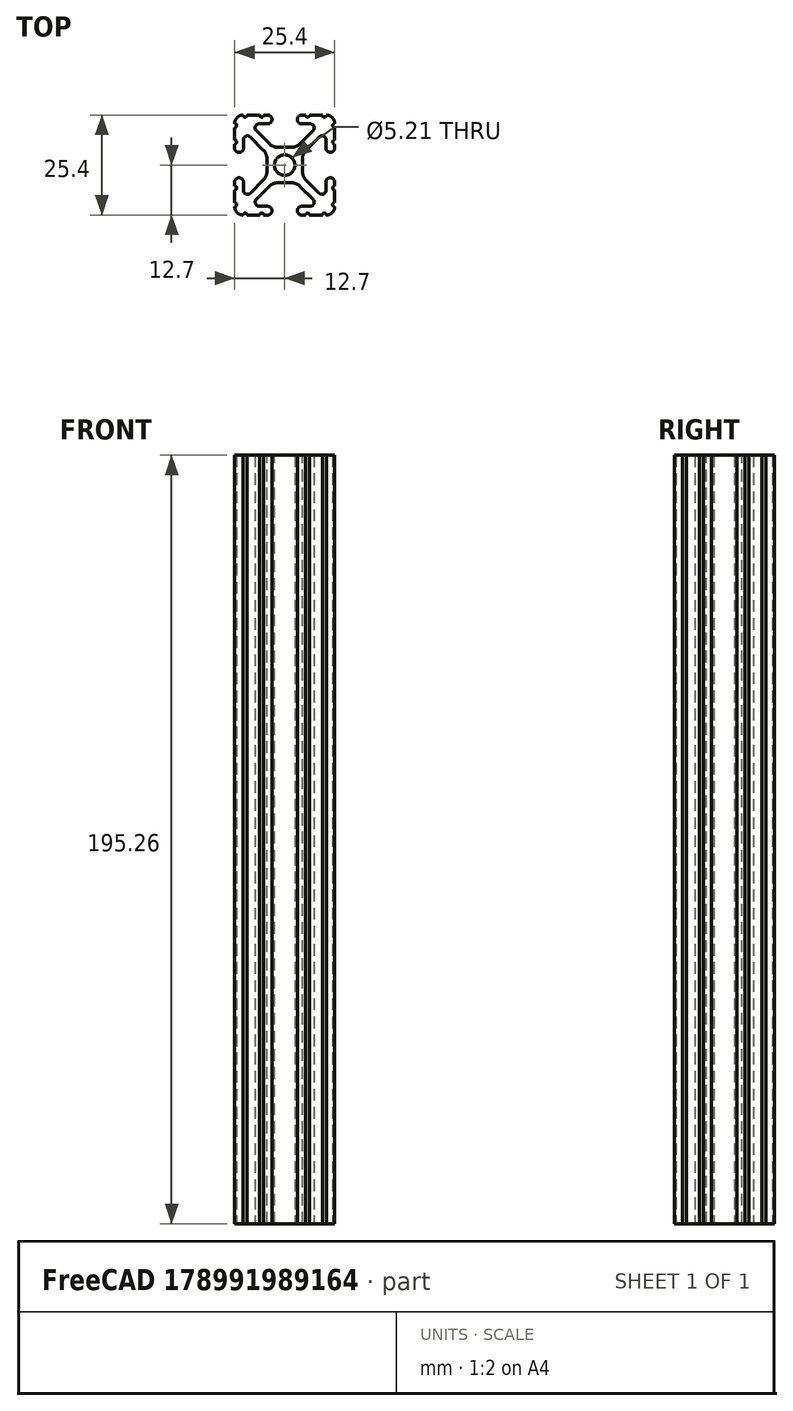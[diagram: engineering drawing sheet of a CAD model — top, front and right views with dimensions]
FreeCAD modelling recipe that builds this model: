
FCSTD DOCUMENT  (FreeCAD 0.19R24267 (Git))
Label: 1010-7p6875
License: All rights reserved
LicenseURL: http://en.wikipedia.org/wiki/All_rights_reserved
objects: Sketcher::SketchObject×1, Part::Extrusion×1
note: 2 computed .brp shape members not serialized (recipe doc carries the construction recipe); baked Part::Feature solids carry a one-line shape summary decoded from their .brp

FEATURE [Sketcher::SketchObject] Sketch097
  FullyConstrained = false
  sketch-geometry (97):
    g0: Circle CenterX=0 CenterY=0 CenterZ=0 NormalX=0 NormalY=0 NormalZ=-1 AngleXU=0 Radius=2.6035
    g1: ArcOfCircle CenterX=12.7 CenterY=5.82508 CenterZ=0 NormalX=0 NormalY=0 NormalZ=1 AngleXU=0 Radius=0.508 StartAngle=1.5708 EndAngle=4.71239
    g2: LineSegment StartX=3.2385 StartY=11.651 StartZ=0 EndX=3.2385 EndY=11.5392 EndZ=0
    g3: LineSegment StartX=6.33313 StartY=-12.7 StartZ=0 EndX=9.55044 EndY=-12.7 EndZ=0
    g4: LineSegment StartX=7.20704 StartY=8.72437 StartZ=0 EndX=3.89827 EndY=5.42317 EndZ=0
    g5: ArcOfCircle CenterX=7.6835 CenterY=1.59319 CenterZ=0 NormalX=0 NormalY=0 NormalZ=1 AngleXU=0 Radius=3.175 StartAngle=2.35505 EndAngle=3.14159
    g6: ArcOfCircle CenterX=-1.70925 CenterY=-7.6708 CenterZ=0 NormalX=0 NormalY=0 NormalZ=1 AngleXU=0 Radius=3.175 StartAngle=1.5708 EndAngle=2.35528
    g7: ArcOfCircle CenterX=11.5392 CenterY=-4.28747 CenterZ=0 NormalX=0 NormalY=0 NormalZ=1 AngleXU=0 Radius=1.04901 StartAngle=1.5708 EndAngle=3.14159
    g8: ArcOfCircle CenterX=12.7 CenterY=-5.82508 CenterZ=0 NormalX=0 NormalY=0 NormalZ=1 AngleXU=0 Radius=0.508 StartAngle=1.5708 EndAngle=4.71239
    g9: LineSegment StartX=4.28751 StartY=10.4902 StartZ=0 EndX=6.47679 EndY=10.4902 EndZ=0
    g10: ArcOfCircle CenterX=4.28751 CenterY=11.651 CenterZ=0 NormalX=0 NormalY=0 NormalZ=1 AngleXU=0 Radius=1.04901 StartAngle=1.5708 EndAngle=3.14159
    g11: ArcOfCircle CenterX=6.47679 CenterY=9.45629 CenterZ=0 NormalX=0 NormalY=0 NormalZ=1 AngleXU=0 Radius=1.03391 StartAngle=5.49664 EndAngle=7.85398
    g12: ArcOfCircle CenterX=4.28751 CenterY=11.5392 CenterZ=0 NormalX=0 NormalY=0 NormalZ=1 AngleXU=0 Radius=1.04901 StartAngle=3.14159 EndAngle=4.71239
    g13: LineSegment StartX=3.95227 StartY=-5.42369 StartZ=0 EndX=7.17965 EndY=-8.64519 EndZ=0
    g14: ArcOfCircle CenterX=11.651 CenterY=4.28747 CenterZ=0 NormalX=0 NormalY=0 NormalZ=1 AngleXU=0 Radius=1.04901 StartAngle=4.71239 EndAngle=6.28319
    g15: ArcOfCircle CenterX=-5.82513 CenterY=-12.7 CenterZ=0 NormalX=0 NormalY=0 NormalZ=1 AngleXU=0 Radius=0.508 StartAngle=0 EndAngle=3.14159
    g16: LineSegment StartX=-6.47679 StartY=10.4902 StartZ=0 EndX=-4.28751 EndY=10.4902 EndZ=0
    g17: ArcOfCircle CenterX=-12.7 CenterY=10.0584 CenterZ=0 NormalX=0 NormalY=0 NormalZ=1 AngleXU=0 Radius=0.508 StartAngle=4.71239 EndAngle=7.85368
    g18: ArcOfCircle CenterX=-12.7 CenterY=5.82508 CenterZ=0 NormalX=0 NormalY=0 NormalZ=1 AngleXU=0 Radius=0.508 StartAngle=4.71239 EndAngle=7.85398
    g19: LineSegment StartX=-11.5392 StartY=-3.23846 StartZ=0 EndX=-11.651 EndY=-3.23846 EndZ=0
    g20: LineSegment StartX=-3.89827 StartY=5.42317 StartZ=0 EndX=-7.20704 EndY=8.72437 EndZ=0
    g21: LineSegment StartX=1.65578 StartY=4.4958 StartZ=0 EndX=-1.65578 EndY=4.4958 EndZ=0
    g22: ArcOfCircle CenterX=-1.65578 CenterY=7.6708 CenterZ=0 NormalX=0 NormalY=0 NormalZ=1 AngleXU=0 Radius=3.175 StartAngle=3.92813 EndAngle=4.71239
    g23: LineSegment StartX=-9.55044 StartY=-12.7 StartZ=0 EndX=-6.33313 EndY=-12.7 EndZ=0
    g24: ArcOfCircle CenterX=-5.82513 CenterY=12.7 CenterZ=0 NormalX=0 NormalY=0 NormalZ=1 AngleXU=0 Radius=0.508 StartAngle=3.14159 EndAngle=6.28319
    g25: ArcOfCircle CenterX=-4.28751 CenterY=11.651 CenterZ=0 NormalX=0 NormalY=0 NormalZ=1 AngleXU=0 Radius=1.04901 StartAngle=0 EndAngle=1.5708
    g26: LineSegment StartX=-12.7 StartY=-4.28747 StartZ=0 EndX=-12.7 EndY=-5.31708 EndZ=0
    g27: ArcOfCircle CenterX=-6.47679 CenterY=9.45629 CenterZ=0 NormalX=0 NormalY=0 NormalZ=1 AngleXU=0 Radius=1.03391 StartAngle=1.5708 EndAngle=3.92813
    g28: ArcOfCircle CenterX=-4.28751 CenterY=11.5392 CenterZ=0 NormalX=0 NormalY=0 NormalZ=1 AngleXU=0 Radius=1.04901 StartAngle=4.71239 EndAngle=6.28319
    g29: LineSegment StartX=-5.44101 StartY=-3.84082 StartZ=0 EndX=-8.73713 EndY=-7.12941 EndZ=0
    g30: ArcOfCircle CenterX=-7.6835 CenterY=-1.59319 CenterZ=0 NormalX=0 NormalY=0 NormalZ=1 AngleXU=0 Radius=3.175 StartAngle=5.49664 EndAngle=6.28319
    g31: LineSegment StartX=-12.7 StartY=5.31708 StartZ=0 EndX=-12.7 EndY=4.28747 EndZ=0
    g32: LineSegment StartX=-8.73713 StartY=7.12941 StartZ=0 EndX=-5.44101 EndY=3.84082 EndZ=0
    g33: LineSegment StartX=-11.651 StartY=3.23846 StartZ=0 EndX=-11.5392 EndY=3.23846 EndZ=0
    g34: ArcOfCircle CenterX=-9.46279 CenterY=-6.40209 CenterZ=0 NormalX=0 NormalY=0 NormalZ=1 AngleXU=0 Radius=1.02741 StartAngle=3.14159 EndAngle=5.49664
    g35: ArcOfCircle CenterX=-10.5918 CenterY=10.5918 CenterZ=0 NormalX=0 NormalY=0 NormalZ=1 AngleXU=0 Radius=2.1082 StartAngle=1.55877 EndAngle=3.15364
    g36: LineSegment StartX=-12.7 StartY=9.5504 StartZ=0 EndX=-12.7 EndY=6.33308 EndZ=0
    g37: LineSegment StartX=-6.33313 StartY=12.7 StartZ=0 EndX=-9.55044 EndY=12.7 EndZ=0
    g38: ArcOfCircle CenterX=-11.5392 CenterY=-4.28747 CenterZ=0 NormalX=0 NormalY=0 NormalZ=1 AngleXU=0 Radius=1.04901 StartAngle=0 EndAngle=1.5708
    g39: LineSegment StartX=4.28751 StartY=-12.7 StartZ=0 EndX=5.31713 EndY=-12.7 EndZ=0
    g40: LineSegment StartX=5.44101 StartY=3.84082 StartZ=0 EndX=8.73713 EndY=7.12941 EndZ=0
    g41: LineSegment StartX=10.4902 StartY=-4.28747 StartZ=0 EndX=10.4902 EndY=-6.40209 EndZ=0
    g42: ArcOfCircle CenterX=9.46279 CenterY=6.40209 CenterZ=0 NormalX=0 NormalY=0 NormalZ=1 AngleXU=0 Radius=1.02741 StartAngle=0 EndAngle=2.35505
    g43: ArcOfCircle CenterX=5.82513 CenterY=-12.7 CenterZ=0 NormalX=0 NormalY=0 NormalZ=1 AngleXU=0 Radius=0.508 StartAngle=0 EndAngle=3.14159
    g44: LineSegment StartX=12.7 StartY=-9.5504 StartZ=0 EndX=12.7 EndY=-6.33308 EndZ=0
    g45: LineSegment StartX=4.5085 StartY=-1.59319 StartZ=0 EndX=4.5085 EndY=1.59319 EndZ=0
    g46: ArcOfCircle CenterX=12.7 CenterY=10.0584 CenterZ=0 NormalX=0 NormalY=0 NormalZ=1 AngleXU=0 Radius=0.508 StartAngle=1.5711 EndAngle=4.71239
    g47: ArcOfCircle CenterX=12.7 CenterY=-10.0584 CenterZ=0 NormalX=0 NormalY=0 NormalZ=1 AngleXU=0 Radius=0.508 StartAngle=1.5708 EndAngle=4.71209
    g48: LineSegment StartX=3.2385 StartY=-11.5392 StartZ=0 EndX=3.2385 EndY=-11.651 EndZ=0
    g49: LineSegment StartX=8.73713 StartY=-7.12941 StartZ=0 EndX=5.44101 EndY=-3.84082 EndZ=0
    g50: ArcOfCircle CenterX=11.651 CenterY=-4.28747 CenterZ=0 NormalX=0 NormalY=0 NormalZ=1 AngleXU=0 Radius=1.04901 StartAngle=0 EndAngle=1.5708
    g51: ArcOfCircle CenterX=1.65578 CenterY=7.6708 CenterZ=0 NormalX=0 NormalY=0 NormalZ=1 AngleXU=0 Radius=3.175 StartAngle=4.71239 EndAngle=5.49664
    g52: ArcOfCircle CenterX=7.6835 CenterY=-1.59319 CenterZ=0 NormalX=0 NormalY=0 NormalZ=1 AngleXU=0 Radius=3.175 StartAngle=3.14159 EndAngle=3.92813
    g53: LineSegment StartX=12.7 StartY=4.28747 StartZ=0 EndX=12.7 EndY=5.31708 EndZ=0
    g54: ArcOfCircle CenterX=6.41641 CenterY=-9.40983 CenterZ=0 NormalX=0 NormalY=0 NormalZ=1 AngleXU=0 Radius=1.08037 StartAngle=4.71239 EndAngle=7.06949
    g55: LineSegment StartX=12.7 StartY=-5.31708 StartZ=0 EndX=12.7 EndY=-4.28747 EndZ=0
    g56: ArcOfCircle CenterX=10.0584 CenterY=-12.7 CenterZ=0 NormalX=0 NormalY=0 NormalZ=1 AngleXU=0 Radius=0.508 StartAngle=0.000300194 EndAngle=3.14159
    g57: ArcOfCircle CenterX=11.5392 CenterY=4.28747 CenterZ=0 NormalX=0 NormalY=0 NormalZ=1 AngleXU=0 Radius=1.04901 StartAngle=3.14159 EndAngle=4.71239
    g58: LineSegment StartX=12.7 StartY=6.33308 StartZ=0 EndX=12.7 EndY=9.5504 EndZ=0
    g59: ArcOfCircle CenterX=4.28751 CenterY=-11.5392 CenterZ=0 NormalX=0 NormalY=0 NormalZ=1 AngleXU=0 Radius=1.04901 StartAngle=1.5708 EndAngle=3.14159
    g60: ArcOfCircle CenterX=10.5918 CenterY=10.5918 CenterZ=0 NormalX=0 NormalY=0 NormalZ=1 AngleXU=0 Radius=2.1082 StartAngle=6.27114 EndAngle=7.86601
    g61: ArcOfCircle CenterX=9.46279 CenterY=-6.40209 CenterZ=0 NormalX=0 NormalY=0 NormalZ=1 AngleXU=0 Radius=1.02741 StartAngle=3.92813 EndAngle=6.28319
    g62: LineSegment StartX=6.41641 StartY=-10.4902 StartZ=0 EndX=4.28751 EndY=-10.4902 EndZ=0
    g63: LineSegment StartX=-10.4902 StartY=-6.40209 StartZ=0 EndX=-10.4902 EndY=-4.28747 EndZ=0
    g64: ArcOfCircle CenterX=-9.46279 CenterY=6.40209 CenterZ=0 NormalX=0 NormalY=0 NormalZ=1 AngleXU=0 Radius=1.02741 StartAngle=0.786542 EndAngle=3.14159
    g65: LineSegment StartX=-10.4902 StartY=4.28747 StartZ=0 EndX=-10.4902 EndY=6.40209 EndZ=0
    g66: LineSegment StartX=-4.5085 StartY=1.59319 StartZ=0 EndX=-4.5085 EndY=-1.59319 EndZ=0
    g67: LineSegment StartX=-4.28751 StartY=12.7 StartZ=0 EndX=-5.31713 EndY=12.7 EndZ=0
    g68: ArcOfCircle CenterX=-11.5392 CenterY=4.28747 CenterZ=0 NormalX=0 NormalY=0 NormalZ=1 AngleXU=0 Radius=1.04901 StartAngle=4.71239 EndAngle=6.28319
    g69: LineSegment StartX=-3.2385 StartY=11.5392 StartZ=0 EndX=-3.2385 EndY=11.651 EndZ=0
    g70: ArcOfCircle CenterX=-11.651 CenterY=4.28747 CenterZ=0 NormalX=0 NormalY=0 NormalZ=1 AngleXU=0 Radius=1.04901 StartAngle=3.14159 EndAngle=4.71239
    g71: ArcOfCircle CenterX=-7.6835 CenterY=1.59319 CenterZ=0 NormalX=0 NormalY=0 NormalZ=1 AngleXU=0 Radius=3.175 StartAngle=0 EndAngle=0.786542
    g72: ArcOfCircle CenterX=-10.0584 CenterY=12.7 CenterZ=0 NormalX=0 NormalY=0 NormalZ=1 AngleXU=0 Radius=0.508 StartAngle=3.14189 EndAngle=6.28319
    g73: LineSegment StartX=-1.70925 StartY=-4.4958 StartZ=0 EndX=1.70925 EndY=-4.4958 EndZ=0
    g74: LineSegment StartX=11.651 StartY=-3.23846 StartZ=0 EndX=11.5392 EndY=-3.23846 EndZ=0
    g75: ArcOfCircle CenterX=-10.5918 CenterY=-10.5918 CenterZ=0 NormalX=0 NormalY=0 NormalZ=1 AngleXU=0 Radius=2.1082 StartAngle=3.12954 EndAngle=4.72442
    g76: ArcOfCircle CenterX=10.5918 CenterY=-10.5918 CenterZ=0 NormalX=0 NormalY=0 NormalZ=1 AngleXU=0 Radius=2.1082 StartAngle=4.70036 EndAngle=6.29523
    g77: ArcOfCircle CenterX=-12.7 CenterY=-5.82508 CenterZ=0 NormalX=0 NormalY=0 NormalZ=1 AngleXU=0 Radius=0.508 StartAngle=4.71239 EndAngle=7.85398
    g78: ArcOfCircle CenterX=5.82513 CenterY=12.7 CenterZ=0 NormalX=0 NormalY=0 NormalZ=1 AngleXU=0 Radius=0.508 StartAngle=3.14159 EndAngle=6.28319
    g79: LineSegment StartX=9.55044 StartY=12.7 StartZ=0 EndX=6.33313 EndY=12.7 EndZ=0
    g80: ArcOfCircle CenterX=10.0584 CenterY=12.7 CenterZ=0 NormalX=0 NormalY=0 NormalZ=1 AngleXU=0 Radius=0.508 StartAngle=3.14159 EndAngle=6.28289
    g81: ArcOfCircle CenterX=1.70925 CenterY=-7.6708 CenterZ=0 NormalX=0 NormalY=0 NormalZ=1 AngleXU=0 Radius=3.175 StartAngle=0.78631 EndAngle=1.5708
    g82: ArcOfCircle CenterX=4.28751 CenterY=-11.651 CenterZ=0 NormalX=0 NormalY=0 NormalZ=1 AngleXU=0 Radius=1.04901 StartAngle=3.14159 EndAngle=4.71239
    g83: LineSegment StartX=5.31713 StartY=12.7 StartZ=0 EndX=4.28751 EndY=12.7 EndZ=0
    g84: LineSegment StartX=10.4902 StartY=6.40209 StartZ=0 EndX=10.4902 EndY=4.28747 EndZ=0
    g85: LineSegment StartX=11.5392 StartY=3.23846 StartZ=0 EndX=11.651 EndY=3.23846 EndZ=0
    g86: ArcOfCircle CenterX=-10.0584 CenterY=-12.7 CenterZ=0 NormalX=0 NormalY=0 NormalZ=1 AngleXU=0 Radius=0.508 StartAngle=0 EndAngle=3.14129
    g87: ArcOfCircle CenterX=-12.7 CenterY=-10.0584 CenterZ=0 NormalX=0 NormalY=0 NormalZ=1 AngleXU=0 Radius=0.508 StartAngle=4.71269 EndAngle=7.85398
    g88: ArcOfCircle CenterX=-4.28751 CenterY=-11.5392 CenterZ=0 NormalX=0 NormalY=0 NormalZ=1 AngleXU=0 Radius=1.04901 StartAngle=0 EndAngle=1.5708
    g89: ArcOfCircle CenterX=-4.28751 CenterY=-11.651 CenterZ=0 NormalX=0 NormalY=0 NormalZ=1 AngleXU=0 Radius=1.04901 StartAngle=4.71239 EndAngle=6.28319
    g90: LineSegment StartX=-12.7 StartY=-6.33308 StartZ=0 EndX=-12.7 EndY=-9.5504 EndZ=0
    g91: ArcOfCircle CenterX=-11.651 CenterY=-4.28747 CenterZ=0 NormalX=0 NormalY=0 NormalZ=1 AngleXU=0 Radius=1.04901 StartAngle=1.5708 EndAngle=3.14159
    g92: LineSegment StartX=-7.17965 StartY=-8.64519 StartZ=0 EndX=-3.95227 EndY=-5.42369 EndZ=0
    g93: LineSegment StartX=-5.31713 StartY=-12.7 StartZ=0 EndX=-4.28751 EndY=-12.7 EndZ=0
    g94: LineSegment StartX=-3.2385 StartY=-11.651 StartZ=0 EndX=-3.2385 EndY=-11.5392 EndZ=0
    g95: ArcOfCircle CenterX=-6.41641 CenterY=-9.40983 CenterZ=0 NormalX=0 NormalY=0 NormalZ=1 AngleXU=0 Radius=1.08037 StartAngle=2.35528 EndAngle=4.71239
    g96: LineSegment StartX=-4.28751 StartY=-10.4902 StartZ=0 EndX=-6.41641 EndY=-10.4902 EndZ=0
FEATURE [Part::Extrusion] Extrude
  Base = -> Sketch097
  Dir = (0,0,1)
  DirMode = 2
  FaceMakerClass = Part::FaceMakerBullseye
  LengthFwd = 195.262
  LengthRev = 0
  Solid = true
  Symmetric = false
